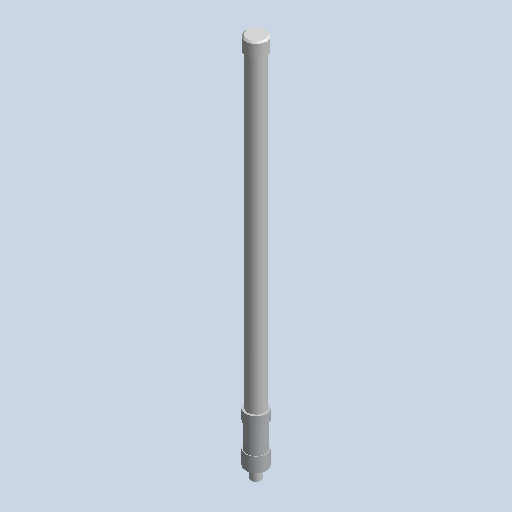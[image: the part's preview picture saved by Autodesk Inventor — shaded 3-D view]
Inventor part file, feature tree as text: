
AUTODESK INVENTOR PART (.ipt)
format: ipt  version: 2022 (Build 260153000, 153)  size: 122,880 bytes
history: native  units: mm (DEFAULTED — no unit token found)
features: other x9, extrude x1, sketch x1, projected_geometry x1
bodies: Body1 (feature_tree)
feature tree (12):
  other  "Sólido1"
  other  "Origen"
  other  "Cut-Extrude4"
  extrude  "Extrusión1"  [1 undecoded]
  other  "Plano YZ"
  other  "Plano XZ"
  other  "Plano XY"
  other  "Eje X"
  other  "Eje Y"
  other  "Eje Z"
  sketch  "Boceto1"  dims[d0=20.0mm d1=0.0mm]
  projected_geometry  "Contorno proyectado1"
note: 1 required parameter value undecoded (feature->parameter linkage not recoverable at this tier; creation-order binding heuristic only, values carry confidence <= 0.55)
